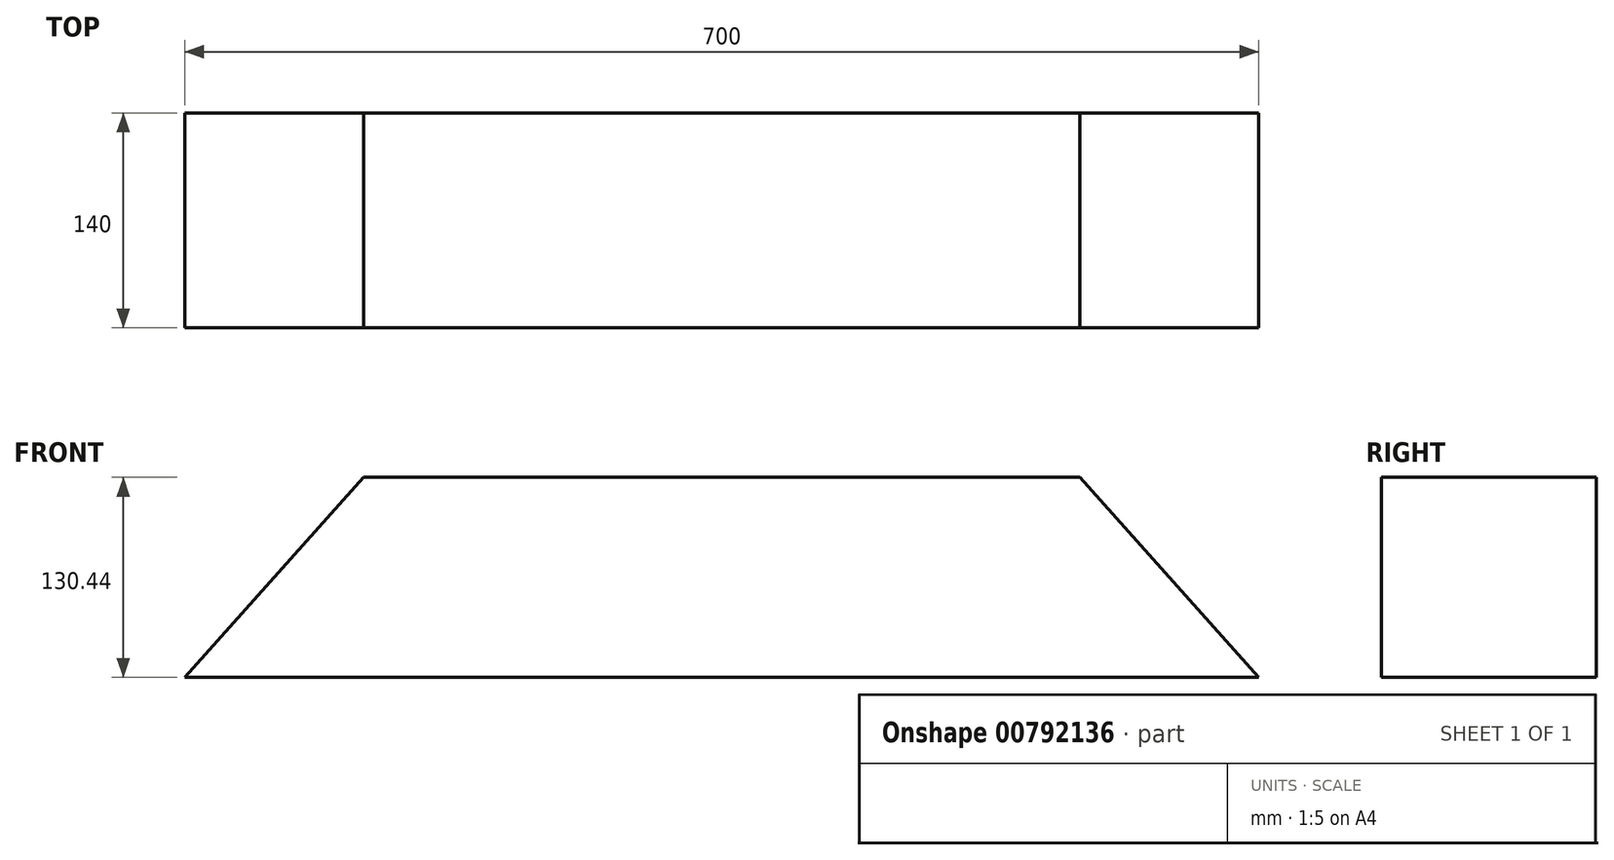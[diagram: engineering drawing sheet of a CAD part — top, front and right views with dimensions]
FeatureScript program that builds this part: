
annotation { "Feature Type Name" : "Feature", "Feature Type Description" : "" }
export const myFeature = defineFeature(function(context is Context, id is Id, definition is map)
    precondition{}
    {
        {
            var Q0;
            Q0=qCreatedBy(makeId("Front.planeOp"),FACE);
            var sketch = newSketch(context, id + "F0", { "sketchPlane" : qUnion([Q0])});
            skLineSegment(sketch, "E0", {"start": v(-350, 0) * mm, "end": v(350, 0) * mm});
            skLineSegment(sketch, "E1", {"start": v(-350, 0) * mm, "end": v(-233.33, 130.44) * mm});
            skLineSegment(sketch, "E2", {"start": v(-233.33, 130.44) * mm, "end": v(-116.67, 0) * mm});
            skLineSegment(sketch, "E3", {"start": v(-116.67, 0) * mm, "end": v(0, 130.44) * mm});
            skLineSegment(sketch, "E4", {"start": v(0, 130.44) * mm, "end": v(116.67, 0) * mm});
            skLineSegment(sketch, "E5", {"start": v(116.67, 0) * mm, "end": v(233.33, 130.44) * mm});
            skLineSegment(sketch, "E6", {"start": v(233.33, 130.44) * mm, "end": v(350, 0) * mm});
            skLineSegment(sketch, "E7", {"start": v(233.33, 130.44) * mm, "end": v(0, 130.44) * mm});
            skLineSegment(sketch, "E8", {"start": v(-233.33, 130.44) * mm, "end": v(0, 130.44) * mm});
            skSolve(sketch);
        }
        {
            var Q0;
            Q0 = qSketchRegion(id + "F0", true);
            extrude(context, id + "F1", {"entities" : qUnion([Q0]), "depth" : 140 * mm, "offsetDistance" : 25 * mm});
        }
    });
